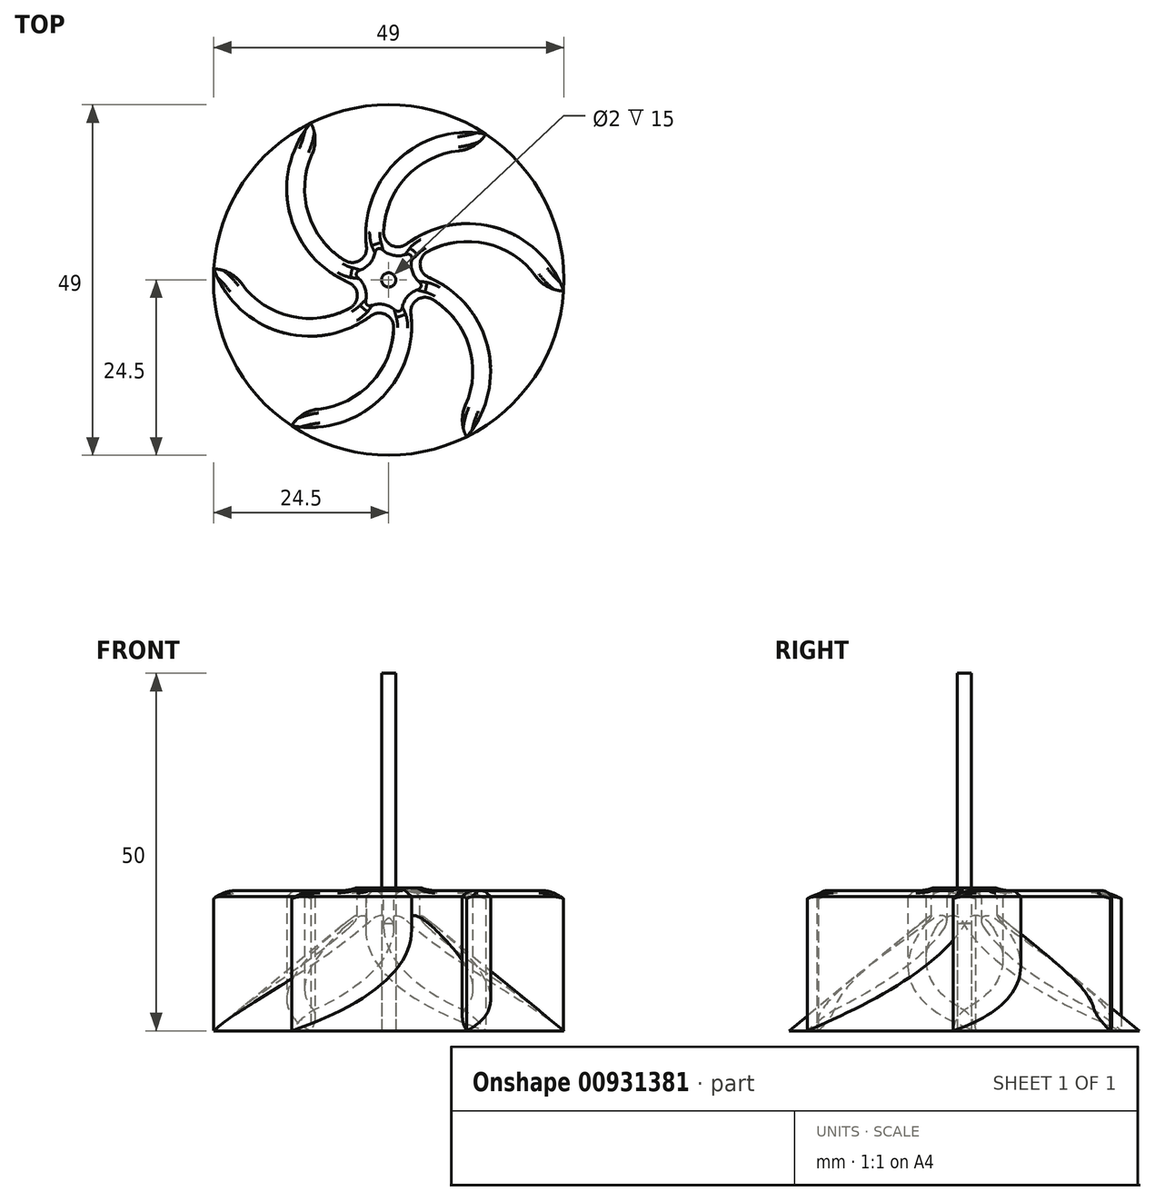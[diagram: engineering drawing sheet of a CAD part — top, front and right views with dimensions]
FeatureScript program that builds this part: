
annotation { "Feature Type Name" : "Feature", "Feature Type Description" : "" }
export const myFeature = defineFeature(function(context is Context, id is Id, definition is map)
    precondition{}
    {
        {
            var Q0;
            Q0=qCreatedBy(makeId("Top.planeOp"),FACE);
            var sketch = newSketch(context, id + "F0", { "sketchPlane" : qUnion([Q0])});
            skCircle(sketch, "E0", {"center": v(0, 0) * mm, "radius": 1.5 * mm});
            skCircle(sketch, "E1", {"center": v(0, 0) * mm, "radius": 24.5 * mm, "construction": true});
            skPoint(sketch, "E2", {"position": v(0, 1.5) * mm});
            skArc(sketch, "E3", {"start": v(10.88, -21.95) * mm, "mid": v(12.93, -6.75) * mm, "end": v(0, 1.5) * mm});
            skArc(sketch, "E4", {"start": v(0, -24.5) * mm, "mid": v(11.74, -13.29) * mm, "end": v(1.07, -1.05) * mm});
            skLineSegment(sketch, "E5", {"start": v(0, 0) * mm, "end": v(1.07, -1.05) * mm, "construction": true});
            skArc(sketch, "E6", {"start": v(10.88, -21.95) * mm, "mid": v(5.59, -23.85) * mm, "end": v(0, -24.5) * mm});
            skLineSegment(sketch, "E7", {"start": v(0, -12.75) * mm, "end": v(13.3, -7.63) * mm, "construction": true});
            skPoint(sketch, "E8", {"position": v(10.97, -8.53) * mm});
            skSolve(sketch);
        }
        {
            var Q0;
            {var subQ0=sQuery(id+"F0.wireOp",EDGE,"E3");Q0=makeQuery(id+"F0.imprint","IMPRINT",FACE,{"disambiguationData":[TD([[makeQuery(id+"F0.imprint","IMPRINT",EDGE,{"derivedFrom":subQ0}),1.0]])]});}
            var Q1;
            {var subQ0=sQuery(id+"F0.wireOp",EDGE,"E0");var subQ1=makeQuery(id+"F0.imprint","INTERSECT",VERTEX,{"derivedFrom":[subQ0,sQuery(id+"F0.wireOp",EDGE,"E3")]});Q1=makeQuery(id+"F0.imprint","IMPRINT",FACE,{"disambiguationData":[TD([[makeQuery(id+"F0.imprint","IMPRINT",EDGE,{"disambiguationData":[TD([[subQ1,-1.0]])],"derivedFrom":subQ0}),1.0]])]});}
            extrude(context, id + "F1", {"entities" : qUnion([Q0, Q1]), "depth" : 20 * mm, "offsetDistance" : 25 * mm});
        }
        {
            var Q0;
            Q0=makeQuery(id+"F1.opExtrude","SWEPT_EDGE",EDGE,{"disambiguationData":[OSD([sQuery(id+"F0.wireOp",EDGE,"E4"),sQuery(id+"F0.wireOp",EDGE,"E6")])]});
            fillet(context, id + "F2", {"entities" : qUnion([Q0]), "radius" : 5 * mm, "tangentPropagation" : true, "allowEdgeOverflow" : false});
        }
        {
            var Q0;
            Q0=qCreatedBy(makeId("Right.planeOp"),FACE);
            var sketch = newSketch(context, id + "F3", { "sketchPlane" : qUnion([Q0])});
            skLineSegment(sketch, "E9", {"start": v(0, 0) * mm, "end": v(0, 10.53) * mm, "construction": true});
            skSolve(sketch);
        }
        {
            var Q0;
            Q0=makeQuery(id+"F1.opExtrude","SWEPT_BODY",BODY,{"disambiguationData":[OSD([sQuery(id+"F0.wireOp",EDGE,"E0"),sQuery(id+"F0.wireOp",EDGE,"E3"),sQuery(id+"F0.wireOp",EDGE,"E4"),sQuery(id+"F0.wireOp",EDGE,"E6")])]});
            var Q1;
            Q1=sQuery(id+"F3.wireOp",EDGE,"E9");
            circularPattern(context, id + "F4", {"operationType" : NewBodyOperationType.ADD, "entities" : qUnion([Q0]), "axis" : qUnion([Q1]), "angle" : 360 * degree, "instanceCount" : 6, "equalSpace" : true});
        }
        {
            var Q0;
            Q0=qCreatedBy(makeId("Front.planeOp"),FACE);
            var sketch = newSketch(context, id + "F5", { "sketchPlane" : qUnion([Q0])});
            skLineSegment(sketch, "E10", {"start": v(0, 0) * mm, "end": v(0, 20) * mm});
            skLineSegment(sketch, "E11", {"start": v(0, 20) * mm, "end": v(24.5, 0) * mm});
            skLineSegment(sketch, "E12", {"start": v(24.5, 0) * mm, "end": v(0, 0) * mm});
            skSolve(sketch);
        }
        {
            var Q0;
            Q0=makeQuery(id+"F5.imprint","IMPRINT",FACE,{"disambiguationData":[TD([[makeQuery(id+"F5.imprint","IMPRINT",EDGE,{"derivedFrom":sQuery(id+"F5.wireOp",EDGE,"E10")}),-1.0]])]});
            var Q1;
            Q1=sQuery(id+"F5.wireOp",EDGE,"E10");
            revolve(context, id + "F6", {"operationType" : NewBodyOperationType.ADD, "surfaceOperationType" : NewSurfaceOperationType.NEW, "entities" : qUnion([Q0]), "axis" : qUnion([Q1]), "revolveType" : RevolveType.FULL});
        }
        {
            var Q0;
            Q0=makeQuery(id+"F4.boolean.opBoolean","INTERSECT",EDGE,{"derivedFrom":[makeQuery(id+"F4.opPattern","COPY",FACE,{"derivedFrom":makeQuery(id+"F1.opExtrude","SWEPT_FACE",FACE,{"disambiguationData":[OSD([sQuery(id+"F0.wireOp",EDGE,"E3")])]}),"instanceName":"4"}),makeQuery(id+"F4.opPattern","COPY",FACE,{"derivedFrom":makeQuery(id+"F1.opExtrude","SWEPT_FACE",FACE,{"disambiguationData":[OSD([sQuery(id+"F0.wireOp",EDGE,"E4")])]}),"instanceName":"5"})]});
            var Q1;
            Q1=makeQuery(id+"F4.boolean.opBoolean","INTERSECT",EDGE,{"derivedFrom":[makeQuery(id+"F1.opExtrude","SWEPT_FACE",FACE,{"disambiguationData":[OSD([sQuery(id+"F0.wireOp",EDGE,"E4")])]}),makeQuery(id+"F4.opPattern","COPY",FACE,{"derivedFrom":makeQuery(id+"F1.opExtrude","SWEPT_FACE",FACE,{"disambiguationData":[OSD([sQuery(id+"F0.wireOp",EDGE,"E3")])]}),"instanceName":"5"})]});
            var Q2;
            Q2=makeQuery(id+"F4.boolean.opBoolean","INTERSECT",EDGE,{"derivedFrom":[makeQuery(id+"F1.opExtrude","SWEPT_FACE",FACE,{"disambiguationData":[OSD([sQuery(id+"F0.wireOp",EDGE,"E3")])]}),makeQuery(id+"F4.opPattern","COPY",FACE,{"derivedFrom":makeQuery(id+"F1.opExtrude","SWEPT_FACE",FACE,{"disambiguationData":[OSD([sQuery(id+"F0.wireOp",EDGE,"E4")])]}),"instanceName":"1"})]});
            var Q3;
            Q3=makeQuery(id+"F4.boolean.opBoolean","INTERSECT",EDGE,{"derivedFrom":[makeQuery(id+"F4.opPattern","COPY",FACE,{"derivedFrom":makeQuery(id+"F1.opExtrude","SWEPT_FACE",FACE,{"disambiguationData":[OSD([sQuery(id+"F0.wireOp",EDGE,"E3")])]}),"instanceName":"1"}),makeQuery(id+"F4.opPattern","COPY",FACE,{"derivedFrom":makeQuery(id+"F1.opExtrude","SWEPT_FACE",FACE,{"disambiguationData":[OSD([sQuery(id+"F0.wireOp",EDGE,"E4")])]}),"instanceName":"2"})]});
            var Q4;
            Q4=makeQuery(id+"F4.boolean.opBoolean","INTERSECT",EDGE,{"derivedFrom":[makeQuery(id+"F4.opPattern","COPY",FACE,{"derivedFrom":makeQuery(id+"F1.opExtrude","SWEPT_FACE",FACE,{"disambiguationData":[OSD([sQuery(id+"F0.wireOp",EDGE,"E3")])]}),"instanceName":"2"}),makeQuery(id+"F4.opPattern","COPY",FACE,{"derivedFrom":makeQuery(id+"F1.opExtrude","SWEPT_FACE",FACE,{"disambiguationData":[OSD([sQuery(id+"F0.wireOp",EDGE,"E4")])]}),"instanceName":"3"})]});
            var Q5;
            Q5=makeQuery(id+"F4.boolean.opBoolean","INTERSECT",EDGE,{"derivedFrom":[makeQuery(id+"F4.opPattern","COPY",FACE,{"derivedFrom":makeQuery(id+"F1.opExtrude","SWEPT_FACE",FACE,{"disambiguationData":[OSD([sQuery(id+"F0.wireOp",EDGE,"E3")])]}),"instanceName":"3"}),makeQuery(id+"F4.opPattern","COPY",FACE,{"derivedFrom":makeQuery(id+"F1.opExtrude","SWEPT_FACE",FACE,{"disambiguationData":[OSD([sQuery(id+"F0.wireOp",EDGE,"E4")])]}),"instanceName":"4"})]});
            fillet(context, id + "F7", {"entities" : qUnion([Q0, Q1, Q2, Q3, Q4, Q5]), "radius" : 2 * mm, "tangentPropagation" : true, "allowEdgeOverflow" : false});
        }
        {
            var Q0;
            {var subQ0=makeQuery(id+"F1.opExtrude","CAP_FACE",FACE,{"disambiguationData":[OSD([sQuery(id+"F0.wireOp",EDGE,"E0"),sQuery(id+"F0.wireOp",EDGE,"E3"),sQuery(id+"F0.wireOp",EDGE,"E4"),sQuery(id+"F0.wireOp",EDGE,"E6")])],"isStart":false});Q0=makeQuery(id+"F4.boolean.opBoolean","MERGE",FACE,{"derivedFrom":[subQ0,makeQuery(id+"F4.opPattern","COPY",FACE,{"derivedFrom":subQ0,"instanceName":"1"}),makeQuery(id+"F4.opPattern","COPY",FACE,{"derivedFrom":subQ0,"instanceName":"2"}),makeQuery(id+"F4.opPattern","COPY",FACE,{"derivedFrom":subQ0,"instanceName":"3"}),makeQuery(id+"F4.opPattern","COPY",FACE,{"derivedFrom":subQ0,"instanceName":"4"}),makeQuery(id+"F4.opPattern","COPY",FACE,{"derivedFrom":subQ0,"instanceName":"5"})]});}
            chamfer(context, id + "F8", {"entities" : qUnion([Q0]), "width" : 1.25 * mm, "tangentPropagation" : true});
        }
        {
            var Q0;
            Q0=makeQuery(id+"F8.opChamfer","BLEND_EDGE",EDGE,{"blendedFrom":[makeQuery(id+"F4.opPattern","COPY",EDGE,{"derivedFrom":makeQuery(id+"F1.opExtrude","CAP_EDGE",EDGE,{"disambiguationData":[OSD([sQuery(id+"F0.wireOp",EDGE,"E3")])],"isStart":false}),"instanceName":"5"}),makeQuery(id+"F4.opPattern","COPY",EDGE,{"derivedFrom":makeQuery(id+"F1.opExtrude","CAP_EDGE",EDGE,{"disambiguationData":[OSD([sQuery(id+"F0.wireOp",EDGE,"E4")])],"isStart":false}),"instanceName":"5"})],"blendedInto":[]});
            var Q1;
            {var subQ0=sQuery(id+"F0.wireOp",EDGE,"E3");var subQ1=sQuery(id+"F0.wireOp",EDGE,"E6");var subQ2=sQuery(id+"F0.wireOp",EDGE,"E4");Q1=makeQuery(id+"F8.opChamfer","BLEND_EDGE",EDGE,{"blendedFrom":[makeQuery(id+"F4.opPattern","COPY",EDGE,{"derivedFrom":makeQuery(id+"F2.opFillet","BLEND_EDGE",EDGE,{"blendedFrom":[makeQuery(id+"F1.opExtrude","SWEPT_EDGE",EDGE,{"disambiguationData":[OSD([subQ2,subQ1])]}),makeQuery(id+"F1.opExtrude","CAP_FACE",FACE,{"disambiguationData":[OSD([sQuery(id+"F0.wireOp",EDGE,"E0"),subQ0,subQ2,subQ1])],"isStart":false})],"blendedInto":[makeQuery(id+"F1.opExtrude","CAP_FACE",FACE,{"disambiguationData":[OSD([sQuery(id+"F0.wireOp",EDGE,"E0"),subQ0,subQ2,subQ1])],"isStart":false})]}),"instanceName":"5"}),makeQuery(id+"F4.opPattern","COPY",EDGE,{"derivedFrom":makeQuery(id+"F1.opExtrude","CAP_EDGE",EDGE,{"disambiguationData":[OSD([subQ0])],"isStart":false}),"instanceName":"5"})],"blendedInto":[]});}
            var Q2;
            {var subQ0=sQuery(id+"F0.wireOp",EDGE,"E3");var subQ1=sQuery(id+"F0.wireOp",EDGE,"E6");var subQ2=sQuery(id+"F0.wireOp",EDGE,"E4");Q2=makeQuery(id+"F8.opChamfer","BLEND_EDGE",EDGE,{"blendedFrom":[makeQuery(id+"F2.opFillet","BLEND_EDGE",EDGE,{"blendedFrom":[makeQuery(id+"F1.opExtrude","SWEPT_EDGE",EDGE,{"disambiguationData":[OSD([subQ2,subQ1])]}),makeQuery(id+"F1.opExtrude","CAP_FACE",FACE,{"disambiguationData":[OSD([sQuery(id+"F0.wireOp",EDGE,"E0"),subQ0,subQ2,subQ1])],"isStart":false})],"blendedInto":[makeQuery(id+"F1.opExtrude","CAP_FACE",FACE,{"disambiguationData":[OSD([sQuery(id+"F0.wireOp",EDGE,"E0"),subQ0,subQ2,subQ1])],"isStart":false})]}),makeQuery(id+"F1.opExtrude","CAP_EDGE",EDGE,{"disambiguationData":[OSD([subQ0])],"isStart":false})],"blendedInto":[]});}
            var Q3;
            Q3=makeQuery(id+"F8.opChamfer","BLEND_EDGE",EDGE,{"blendedFrom":[makeQuery(id+"F1.opExtrude","CAP_EDGE",EDGE,{"disambiguationData":[OSD([sQuery(id+"F0.wireOp",EDGE,"E3")])],"isStart":false}),makeQuery(id+"F1.opExtrude","CAP_EDGE",EDGE,{"disambiguationData":[OSD([sQuery(id+"F0.wireOp",EDGE,"E4")])],"isStart":false})],"blendedInto":[]});
            var Q4;
            Q4=makeQuery(id+"F8.opChamfer","BLEND_EDGE",EDGE,{"blendedFrom":[makeQuery(id+"F4.opPattern","COPY",EDGE,{"derivedFrom":makeQuery(id+"F1.opExtrude","CAP_EDGE",EDGE,{"disambiguationData":[OSD([sQuery(id+"F0.wireOp",EDGE,"E3")])],"isStart":false}),"instanceName":"4"}),makeQuery(id+"F4.opPattern","COPY",EDGE,{"derivedFrom":makeQuery(id+"F1.opExtrude","CAP_EDGE",EDGE,{"disambiguationData":[OSD([sQuery(id+"F0.wireOp",EDGE,"E4")])],"isStart":false}),"instanceName":"4"})],"blendedInto":[]});
            var Q5;
            {var subQ0=sQuery(id+"F0.wireOp",EDGE,"E3");var subQ1=sQuery(id+"F0.wireOp",EDGE,"E6");var subQ2=sQuery(id+"F0.wireOp",EDGE,"E4");Q5=makeQuery(id+"F8.opChamfer","BLEND_EDGE",EDGE,{"blendedFrom":[makeQuery(id+"F4.opPattern","COPY",EDGE,{"derivedFrom":makeQuery(id+"F2.opFillet","BLEND_EDGE",EDGE,{"blendedFrom":[makeQuery(id+"F1.opExtrude","SWEPT_EDGE",EDGE,{"disambiguationData":[OSD([subQ2,subQ1])]}),makeQuery(id+"F1.opExtrude","CAP_FACE",FACE,{"disambiguationData":[OSD([sQuery(id+"F0.wireOp",EDGE,"E0"),subQ0,subQ2,subQ1])],"isStart":false})],"blendedInto":[makeQuery(id+"F1.opExtrude","CAP_FACE",FACE,{"disambiguationData":[OSD([sQuery(id+"F0.wireOp",EDGE,"E0"),subQ0,subQ2,subQ1])],"isStart":false})]}),"instanceName":"4"}),makeQuery(id+"F4.opPattern","COPY",EDGE,{"derivedFrom":makeQuery(id+"F1.opExtrude","CAP_EDGE",EDGE,{"disambiguationData":[OSD([subQ0])],"isStart":false}),"instanceName":"4"})],"blendedInto":[]});}
            var Q6;
            Q6=makeQuery(id+"F8.opChamfer","BLEND_EDGE",EDGE,{"blendedFrom":[makeQuery(id+"F4.opPattern","COPY",EDGE,{"derivedFrom":makeQuery(id+"F1.opExtrude","CAP_EDGE",EDGE,{"disambiguationData":[OSD([sQuery(id+"F0.wireOp",EDGE,"E3")])],"isStart":false}),"instanceName":"2"}),makeQuery(id+"F4.opPattern","COPY",EDGE,{"derivedFrom":makeQuery(id+"F1.opExtrude","CAP_EDGE",EDGE,{"disambiguationData":[OSD([sQuery(id+"F0.wireOp",EDGE,"E4")])],"isStart":false}),"instanceName":"2"})],"blendedInto":[]});
            var Q7;
            Q7=makeQuery(id+"F8.opChamfer","BLEND_EDGE",EDGE,{"blendedFrom":[makeQuery(id+"F4.opPattern","COPY",EDGE,{"derivedFrom":makeQuery(id+"F1.opExtrude","CAP_EDGE",EDGE,{"disambiguationData":[OSD([sQuery(id+"F0.wireOp",EDGE,"E3")])],"isStart":false}),"instanceName":"1"}),makeQuery(id+"F4.opPattern","COPY",EDGE,{"derivedFrom":makeQuery(id+"F1.opExtrude","CAP_EDGE",EDGE,{"disambiguationData":[OSD([sQuery(id+"F0.wireOp",EDGE,"E4")])],"isStart":false}),"instanceName":"1"})],"blendedInto":[]});
            var Q8;
            {var subQ0=sQuery(id+"F0.wireOp",EDGE,"E3");var subQ1=sQuery(id+"F0.wireOp",EDGE,"E6");var subQ2=sQuery(id+"F0.wireOp",EDGE,"E4");Q8=makeQuery(id+"F8.opChamfer","BLEND_EDGE",EDGE,{"blendedFrom":[makeQuery(id+"F4.opPattern","COPY",EDGE,{"derivedFrom":makeQuery(id+"F2.opFillet","BLEND_EDGE",EDGE,{"blendedFrom":[makeQuery(id+"F1.opExtrude","SWEPT_EDGE",EDGE,{"disambiguationData":[OSD([subQ2,subQ1])]}),makeQuery(id+"F1.opExtrude","CAP_FACE",FACE,{"disambiguationData":[OSD([sQuery(id+"F0.wireOp",EDGE,"E0"),subQ0,subQ2,subQ1])],"isStart":false})],"blendedInto":[makeQuery(id+"F1.opExtrude","CAP_FACE",FACE,{"disambiguationData":[OSD([sQuery(id+"F0.wireOp",EDGE,"E0"),subQ0,subQ2,subQ1])],"isStart":false})]}),"instanceName":"1"}),makeQuery(id+"F4.opPattern","COPY",EDGE,{"derivedFrom":makeQuery(id+"F1.opExtrude","CAP_EDGE",EDGE,{"disambiguationData":[OSD([subQ0])],"isStart":false}),"instanceName":"1"})],"blendedInto":[]});}
            var Q9;
            {var subQ0=sQuery(id+"F0.wireOp",EDGE,"E3");var subQ1=sQuery(id+"F0.wireOp",EDGE,"E6");var subQ2=sQuery(id+"F0.wireOp",EDGE,"E4");Q9=makeQuery(id+"F8.opChamfer","BLEND_EDGE",EDGE,{"blendedFrom":[makeQuery(id+"F4.opPattern","COPY",EDGE,{"derivedFrom":makeQuery(id+"F2.opFillet","BLEND_EDGE",EDGE,{"blendedFrom":[makeQuery(id+"F1.opExtrude","SWEPT_EDGE",EDGE,{"disambiguationData":[OSD([subQ2,subQ1])]}),makeQuery(id+"F1.opExtrude","CAP_FACE",FACE,{"disambiguationData":[OSD([sQuery(id+"F0.wireOp",EDGE,"E0"),subQ0,subQ2,subQ1])],"isStart":false})],"blendedInto":[makeQuery(id+"F1.opExtrude","CAP_FACE",FACE,{"disambiguationData":[OSD([sQuery(id+"F0.wireOp",EDGE,"E0"),subQ0,subQ2,subQ1])],"isStart":false})]}),"instanceName":"3"}),makeQuery(id+"F4.opPattern","COPY",EDGE,{"derivedFrom":makeQuery(id+"F1.opExtrude","CAP_EDGE",EDGE,{"disambiguationData":[OSD([subQ0])],"isStart":false}),"instanceName":"3"})],"blendedInto":[]});}
            var Q10;
            Q10=makeQuery(id+"F8.opChamfer","BLEND_EDGE",EDGE,{"blendedFrom":[makeQuery(id+"F4.opPattern","COPY",EDGE,{"derivedFrom":makeQuery(id+"F1.opExtrude","CAP_EDGE",EDGE,{"disambiguationData":[OSD([sQuery(id+"F0.wireOp",EDGE,"E3")])],"isStart":false}),"instanceName":"3"}),makeQuery(id+"F4.opPattern","COPY",EDGE,{"derivedFrom":makeQuery(id+"F1.opExtrude","CAP_EDGE",EDGE,{"disambiguationData":[OSD([sQuery(id+"F0.wireOp",EDGE,"E4")])],"isStart":false}),"instanceName":"3"})],"blendedInto":[]});
            var Q11;
            {var subQ0=sQuery(id+"F0.wireOp",EDGE,"E3");var subQ1=sQuery(id+"F0.wireOp",EDGE,"E6");var subQ2=sQuery(id+"F0.wireOp",EDGE,"E4");Q11=makeQuery(id+"F8.opChamfer","BLEND_EDGE",EDGE,{"blendedFrom":[makeQuery(id+"F4.opPattern","COPY",EDGE,{"derivedFrom":makeQuery(id+"F2.opFillet","BLEND_EDGE",EDGE,{"blendedFrom":[makeQuery(id+"F1.opExtrude","SWEPT_EDGE",EDGE,{"disambiguationData":[OSD([subQ2,subQ1])]}),makeQuery(id+"F1.opExtrude","CAP_FACE",FACE,{"disambiguationData":[OSD([sQuery(id+"F0.wireOp",EDGE,"E0"),subQ0,subQ2,subQ1])],"isStart":false})],"blendedInto":[makeQuery(id+"F1.opExtrude","CAP_FACE",FACE,{"disambiguationData":[OSD([sQuery(id+"F0.wireOp",EDGE,"E0"),subQ0,subQ2,subQ1])],"isStart":false})]}),"instanceName":"2"}),makeQuery(id+"F4.opPattern","COPY",EDGE,{"derivedFrom":makeQuery(id+"F1.opExtrude","CAP_EDGE",EDGE,{"disambiguationData":[OSD([subQ0])],"isStart":false}),"instanceName":"2"})],"blendedInto":[]});}
            fillet(context, id + "F9", {"entities" : qUnion([Q0, Q1, Q2, Q3, Q4, Q5, Q6, Q7, Q8, Q9, Q10, Q11]), "radius" : 1 * mm, "tangentPropagation" : true, "allowEdgeOverflow" : false});
        }
        {
            var Q0;
            {var subQ0=makeQuery(id+"F1.opExtrude","CAP_FACE",FACE,{"disambiguationData":[OSD([sQuery(id+"F0.wireOp",EDGE,"E0"),sQuery(id+"F0.wireOp",EDGE,"E3"),sQuery(id+"F0.wireOp",EDGE,"E4"),sQuery(id+"F0.wireOp",EDGE,"E6")])],"isStart":true});Q0=makeQuery(id+"F6.boolean.opBoolean","MERGE",FACE,{"derivedFrom":[makeQuery(id+"F4.boolean.opBoolean","MERGE",FACE,{"derivedFrom":[subQ0,makeQuery(id+"F4.opPattern","COPY",FACE,{"derivedFrom":subQ0,"instanceName":"1"}),makeQuery(id+"F4.opPattern","COPY",FACE,{"derivedFrom":subQ0,"instanceName":"2"}),makeQuery(id+"F4.opPattern","COPY",FACE,{"derivedFrom":subQ0,"instanceName":"3"}),makeQuery(id+"F4.opPattern","COPY",FACE,{"derivedFrom":subQ0,"instanceName":"4"}),makeQuery(id+"F4.opPattern","COPY",FACE,{"derivedFrom":subQ0,"instanceName":"5"})]}),makeQuery(id+"F6.opRevolve","SWEPT_FACE",FACE,{"disambiguationData":[OSD([sQuery(id+"F5.wireOp",EDGE,"E12")])]})]});}
            var sketch = newSketch(context, id + "F10", { "sketchPlane" : qUnion([Q0])});
            skCircle(sketch, "E13", {"center": v(0, 0) * mm, "radius": 1 * mm});
            skSolve(sketch);
        }
        {
            var Q0;
            Q0 = qSketchRegion(id + "F10", true);
            extrude(context, id + "F11", {"entities" : qUnion([Q0]), "operationType" : NewBodyOperationType.REMOVE, "oppositeDirection" : true, "depth" : 15 * mm, "offsetDistance" : 25 * mm});
        }
        {
            var Q0;
            Q0=qCreatedBy(makeId("Top.planeOp"),FACE);
            var sketch = newSketch(context, id + "F12", { "sketchPlane" : qUnion([Q0])});
            skCircle(sketch, "E14", {"center": v(0, 0) * mm, "radius": 1 * mm});
            skSolve(sketch);
        }
        {
            var Q0;
            Q0 = qSketchRegion(id + "F12", true);
            extrude(context, id + "F13", {"entities" : qUnion([Q0]), "depth" : 50 * mm, "offsetDistance" : 25 * mm});
        }
    });
